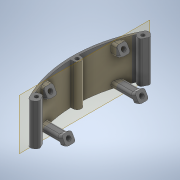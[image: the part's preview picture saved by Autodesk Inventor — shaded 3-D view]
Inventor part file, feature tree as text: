
AUTODESK INVENTOR PART (.ipt)
format: ipt  version: 2020 (Build 240168000, 168)  size: 1,333,248 bytes
history: native  units: mm
features: projected_geometry x30, extrude x17, sketch x12, other x9, fillet x1
ambient origin geometry x8: Origin, YZ Plane, XZ Plane, XY Plane, X Axis, Y Axis, Z Axis, Center Point
bodies: Body1 (feature_tree)
feature tree (69):
  other  "Твердое тело1"
  extrude  "outer"  TaperAngle=45.0deg  [1 undecoded]
  extrude  "inner"  Depth=7.0mm
  sketch  "Эскиз3"
  extrude  "Выдавливание3"  Depth=20.0mm
  extrude  "Выдавливание4"  Depth=7.0mm
  sketch  "Эскиз4"
  extrude  "Выдавливание5"  Depth=3.2mm
  extrude  "Выдавливание6"  Depth=59.0mm
  sketch  "Эскиз5"
  extrude  "Выдавливание7"  Depth=83.0mm
  extrude  "Выдавливание8"  Depth=69.0mm
  sketch  "Эскиз6"
  extrude  "Выдавливание9"  Depth=55.0mm
  extrude  "Выдавливание10"  Depth=3.0mm
  fillet  "Сопряжение1"  Radius=8.0mm
  other  "РабПлоскость2"
  other  "РабПлоскость3"
  sketch  "Эскиз10"
  sketch  "Эскиз11"
  other  "РабПлоскость4"
  other  "РабПлоскость5"
  other  "РабОсь2"
  other  "РабОсь1"
  sketch  "Эскиз12"
  extrude  "Выдавливание12"  Depth=5.0mm
  sketch  "Эскиз8"
  extrude  "asterisk"  Depth=2.0mm
  other  "РабПлоскость7"
  sketch  "Эскиз13"
  extrude  "Выдавливание13"  Depth=40.0mm TaperAngle=360.0deg
  extrude  "Выдавливание14"  Depth=2.0mm
  extrude  "Выдавливание15"  Depth=105.0mm
  extrude  "Выдавливание16"  Depth=2.0mm
  extrude  "Выдавливание17"  Depth=2.0mm TaperAngle=0.0deg
  sketch  "Эскиз1"
  sketch  "Эскиз2"
  projected_geometry  "Спроецированная петля1"
  projected_geometry  "Спроецированная петля2"
  projected_geometry  "Спроецированная петля3"
  projected_geometry  "Спроецированная петля4"
  projected_geometry  "Спроецированная петля5"
  projected_geometry  "Спроецированная петля8"
  projected_geometry  "Спроецированная петля9"
  projected_geometry  "Спроецированная петля10"
  projected_geometry  "Спроецированная петля11"
  projected_geometry  "Спроецированная петля12"
  other  "РабПлоскость6"
  projected_geometry  "Спроецированная петля13"
  projected_geometry  "Спроецированная петля14"
  projected_geometry  "Спроецированная петля15"
  projected_geometry  "Спроецированная петля16"
  projected_geometry  "Спроецированная петля17"
  projected_geometry  "Спроецированная петля18"
  projected_geometry  "Спроецированная петля19"
  projected_geometry  "Спроецированная петля20"
  projected_geometry  "Спроецированная петля21"
  projected_geometry  "Спроецированная петля22"
  projected_geometry  "Спроецированная петля23"
  projected_geometry  "Спроецированная петля24"
  projected_geometry  "Спроецированная петля25"
  projected_geometry  "Спроецированная петля26"
  projected_geometry  "Спроецированная петля27"
  projected_geometry  "Спроецированная петля28"
  projected_geometry  "Спроецированная петля29"
  projected_geometry  "Спроецированная петля30"
  projected_geometry  "Спроецированная петля31"
  projected_geometry  "Спроецированная петля32"
  sketch  "Эскиз14"
note: 1 required parameter value undecoded (feature->parameter linkage not recoverable at this tier; creation-order binding heuristic only, values carry confidence <= 0.55)
